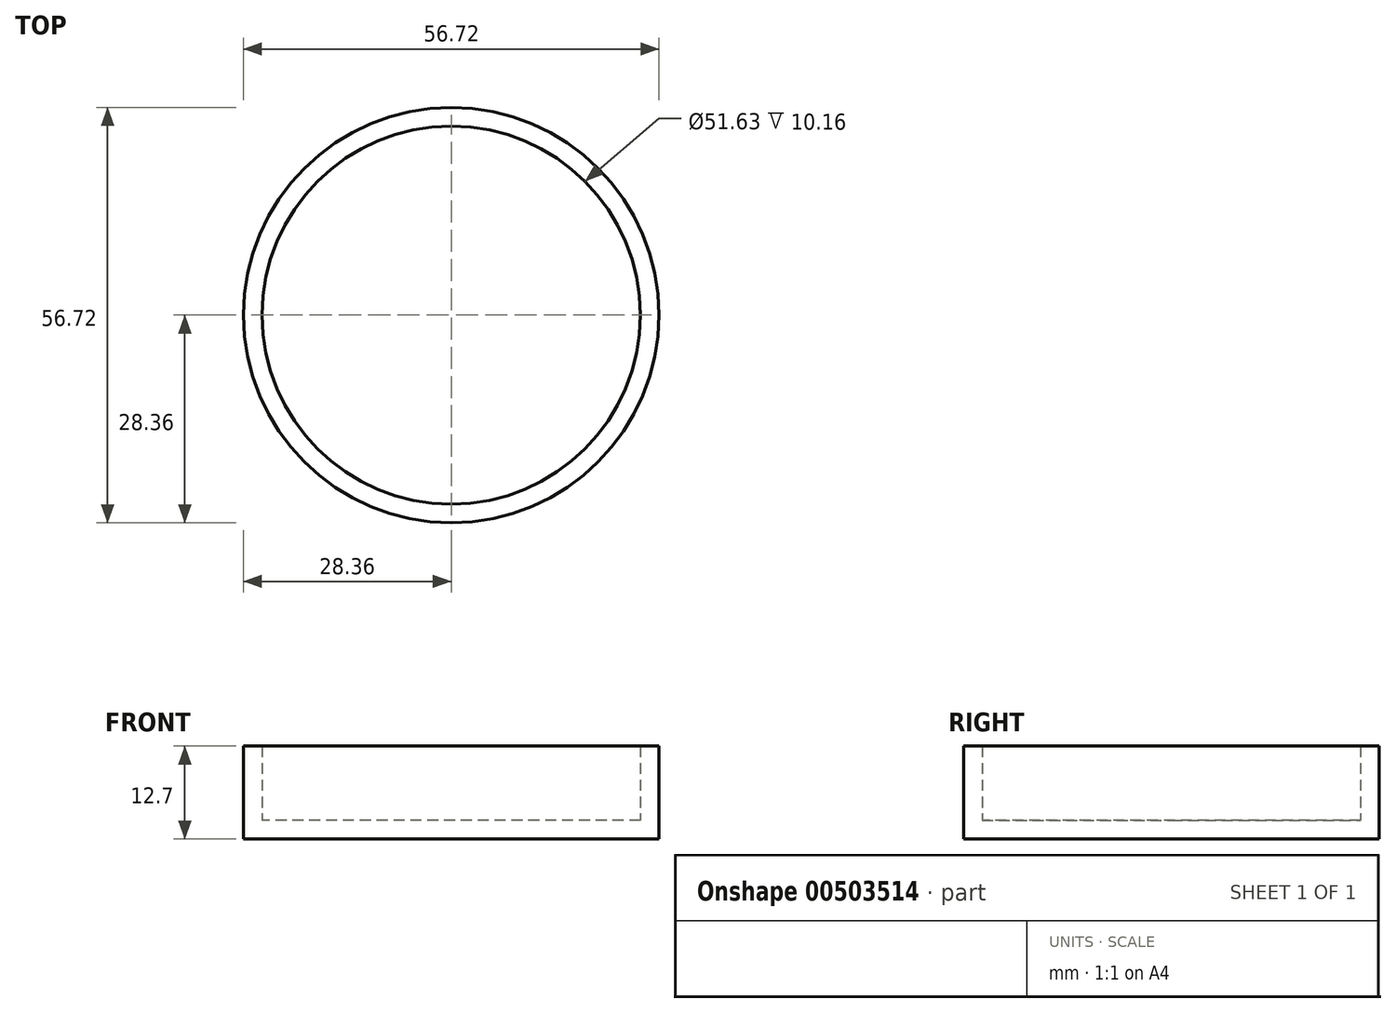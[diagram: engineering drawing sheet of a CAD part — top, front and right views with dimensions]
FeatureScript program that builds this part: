
annotation { "Feature Type Name" : "Feature", "Feature Type Description" : "" }
export const myFeature = defineFeature(function(context is Context, id is Id, definition is map)
    precondition{}
    {
        {
            var Q0;
            Q0=qCreatedBy(makeId("Top.planeOp"),FACE);
            var sketch = newSketch(context, id + "F0", { "sketchPlane" : qUnion([Q0])});
            skCircle(sketch, "E0", {"center": v(0, 0) * mm, "radius": 28.36 * mm});
            skSolve(sketch);
        }
        {
            var Q0;
            Q0 = qSketchRegion(id + "F0", true);
            var Q1;
            Q1=makeQuery(id+"F0.imprint","IMPRINT",FACE,{"disambiguationData":[TD([[makeQuery(id+"F0.imprint","IMPRINT",EDGE,{"derivedFrom":sQuery(id+"F0.wireOp",EDGE,"E0")}),1.0]])]});
            extrude(context, id + "F1", {"entities" : qUnion([Q0, Q1]), "depth" : 12.7 * mm});
        }
        {
            var Q0;
            Q0=makeQuery(id+"F1.opExtrude","CAP_FACE",FACE,{"disambiguationData":[OSD([sQuery(id+"F0.wireOp",EDGE,"E0")])],"isStart":false});
            shell(context, id + "F2", {"entities" : qUnion([Q0]), "thickness" : 2.54 * mm});
        }
    });
